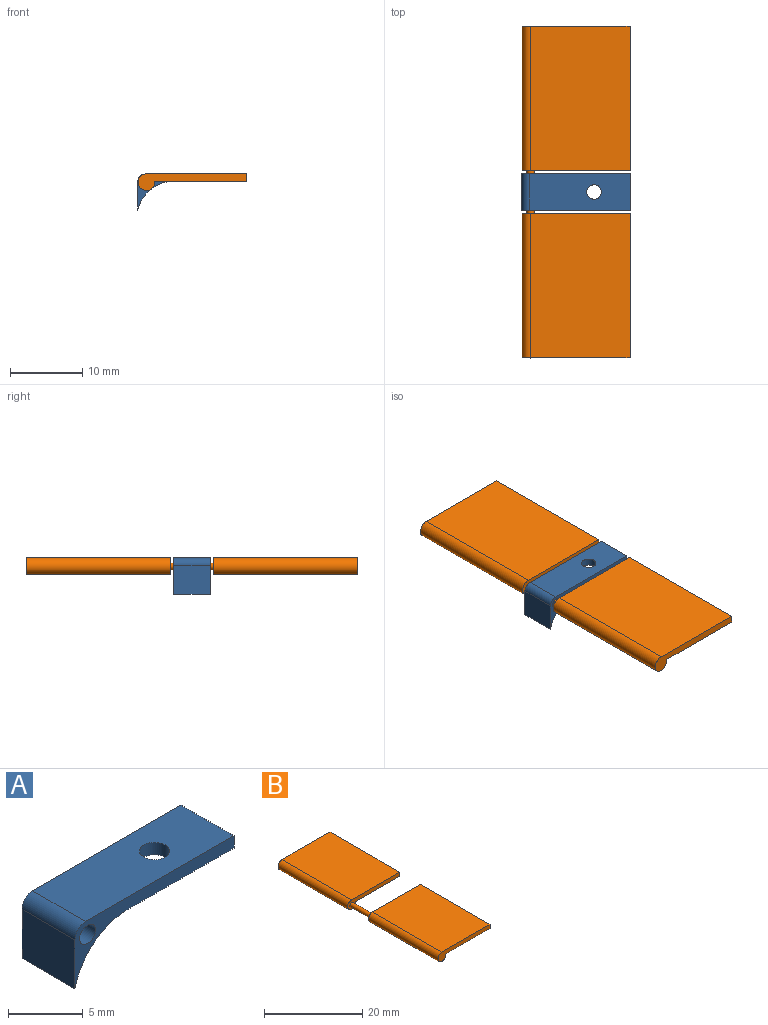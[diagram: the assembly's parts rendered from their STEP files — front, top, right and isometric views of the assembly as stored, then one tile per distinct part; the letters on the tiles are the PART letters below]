
ASSEMBLY  parts=2 mates=1
PART A: 10 faces, bbox 15x5x5 mm
  f0: plane 14x5mm, normal (0,0,1), area 66.9mm2, adj f4,f6,f7,f8,f9
  f1: plane 5x4mm, normal (-1,0,0), area 20mm2, adj f2,f6,f7,f9
  f2: cylinder r=5.12mm len=5mm, axis (0,1,0), area 34.6mm2, adj f1,f3,f6,f7
  f3: plane 10x5mm, normal (0,0,-1), area 46.9mm2, adj f2,f4,f6,f7,f8
  f4: plane 5x1mm, normal (1,0,0), area 5mm2, adj f0,f3,f6,f7
  f5: cylinder r=0.75mm len=5mm, axis (0,1,0), area 23.6mm2, adj f6,f7
  f6: plane 15x5mm, normal (0,-1,0), area 18.1mm2, adj f0,f1,f2,f3,f4,f5,f9
  f7: plane 15x5mm, normal (0,1,0), area 18.1mm2, adj f0,f1,f2,f3,f4,f5,f9
  f8: cylinder r=1mm len=2mm, axis (0,0,1), area 6.3mm2, adj f0,f3
  f9: cylinder r=1mm len=5mm, axis (0,1,0), area 7.9mm2, adj f0,f1,f6,f7
PART B: 13 faces, bbox 15x46x2.3 mm
  f0: plane 20x13.8mm, normal (0,0,1), area 276mm2, adj f2,f3,f4,f6
  f1: plane 20x12.66mm, normal (0,0,-1), area 253.2mm2, adj f2,f3,f4,f6
  f2: plane 20x1mm, normal (1,0,0), area 20mm2, adj f0,f1,f4,f6
  f3: cylinder r=1.15mm len=20mm, axis (0,1,0), area 111.4mm2, adj f0,f1,f4,f6
  f4: plane 14.95x2.3mm, normal (0,1,0), area 17.1mm2, adj f0,f1,f2,f3
  f5: cylinder r=0.5mm len=6mm, axis (0,-1,0), area 18.8mm2, adj f6,f7
  f6: plane 14.95x2.3mm, normal (0,-1,0), area 16.3mm2, adj f0,f1,f2,f3,f5
  f7: plane 14.95x2.3mm, normal (0,1,0), area 16.3mm2, adj f5,f9,f10,f11,f12
  f8: plane 14.95x2.3mm, normal (0,-1,0), area 17.1mm2, adj f9,f10,f11,f12
  f9: plane 20x1mm, normal (1,0,0), area 20mm2, adj f7,f8,f10,f12
  f10: plane 20x12.66mm, normal (0,0,-1), area 253.2mm2, adj f7,f8,f9,f11
  f11: cylinder r=1.15mm len=20mm, axis (0,1,0), area 111.4mm2, adj f7,f8,f10,f12
  f12: plane 20x13.8mm, normal (0,0,1), area 276mm2, adj f7,f8,f9,f11
PLACE A t=(-9.66,5.39,18.75)mm
PLACE B t=(-8.47,-0.11,18.61)mm
MATE cylindrical B.f5 <-> A.f5  axis (0,-1,0) through (-8.47,2.89,18.61)mm
